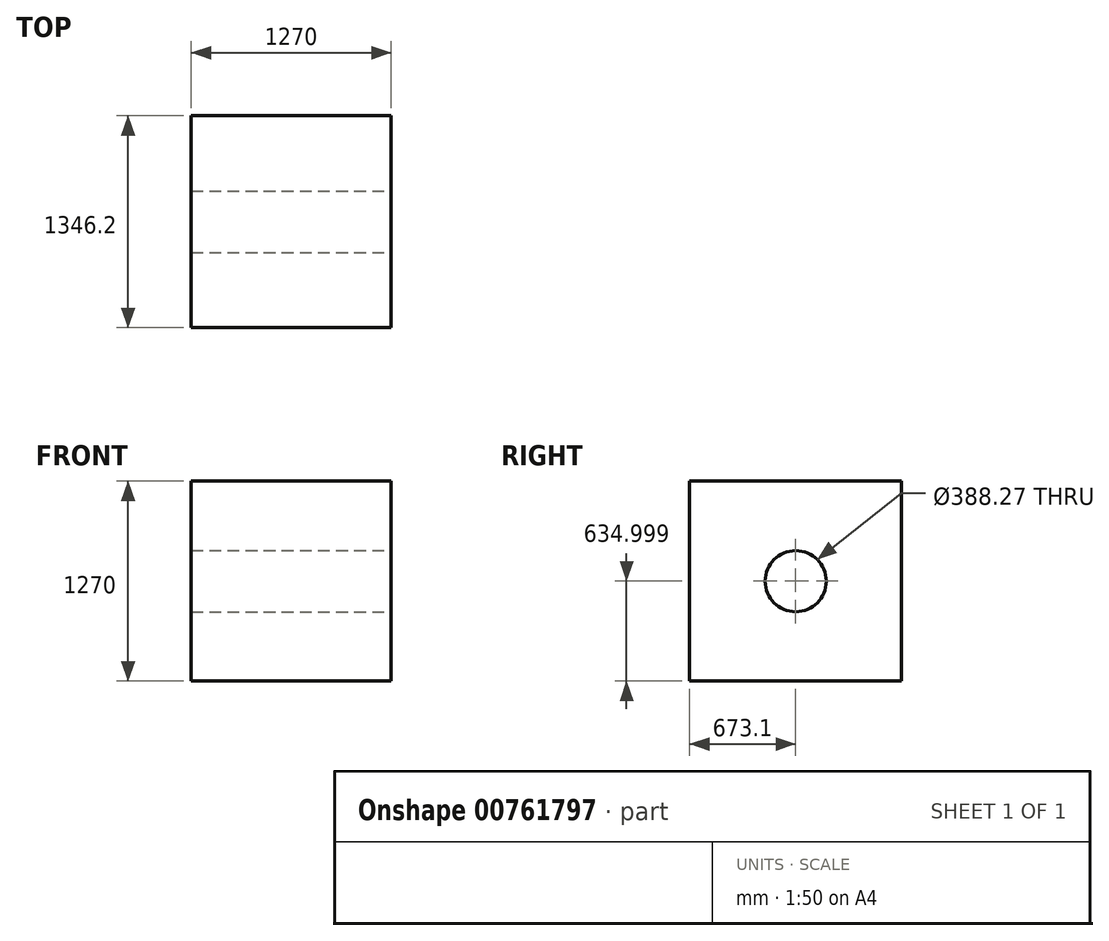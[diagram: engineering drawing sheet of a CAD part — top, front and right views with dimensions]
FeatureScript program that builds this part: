
annotation { "Feature Type Name" : "Feature", "Feature Type Description" : "" }
export const myFeature = defineFeature(function(context is Context, id is Id, definition is map)
    precondition{}
    {
        {
            var Q0;
            Q0=qCreatedBy(makeId("Front.planeOp"),FACE);
            var sketch = newSketch(context, id + "F0", { "sketchPlane" : qUnion([Q0])});
            skLineSegment(sketch, "E0.bottom", {"start": v(-52.99, 1250.98) * mm, "end": v(1217.01, 1250.98) * mm});
            skLineSegment(sketch, "E0.top", {"start": v(-52.99, -19.02) * mm, "end": v(1217.01, -19.02) * mm});
            skLineSegment(sketch, "E0.left", {"start": v(-52.99, 1250.98) * mm, "end": v(-52.99, -19.02) * mm});
            skLineSegment(sketch, "E0.right", {"start": v(1217.01, 1250.98) * mm, "end": v(1217.01, -19.02) * mm});
            skSolve(sketch);
        }
        {
            var Q0;
            Q0=makeQuery(id+"F0.imprint","IMPRINT",FACE,{"disambiguationData":[TD([[makeQuery(id+"F0.imprint","IMPRINT",EDGE,{"derivedFrom":sQuery(id+"F0.wireOp",EDGE,"E0.bottom")}),-1.0]])]});
            extrude(context, id + "F1", {"entities" : qUnion([Q0]), "depth" : 76.2 * mm, "offsetDistance" : 25.4 * mm});
        }
        {
            var Q0;
            Q0=makeQuery(id+"F1.opExtrude","CAP_FACE",FACE,{"disambiguationData":[OSD([sQuery(id+"F0.wireOp",EDGE,"E0.bottom"),sQuery(id+"F0.wireOp",EDGE,"E0.top"),sQuery(id+"F0.wireOp",EDGE,"E0.left"),sQuery(id+"F0.wireOp",EDGE,"E0.right")])],"isStart":true});
            var Q1;
            Q1=makeQuery(id+"F1.opExtrude","CAP_FACE",FACE,{"disambiguationData":[OSD([sQuery(id+"F0.wireOp",EDGE,"E0.bottom"),sQuery(id+"F0.wireOp",EDGE,"E0.top"),sQuery(id+"F0.wireOp",EDGE,"E0.left"),sQuery(id+"F0.wireOp",EDGE,"E0.right")])],"isStart":false});
            extrude(context, id + "F2", {"entities" : qUnion([Q0, Q1]), "operationType" : NewBodyOperationType.ADD, "depth" : 1270 * mm, "offsetDistance" : 25.4 * mm});
        }
        {
            var Q0;
            {var subQ0=sQuery(id+"F0.wireOp",EDGE,"E0.right");Q0=makeQuery(id+"F2.boolean.opBoolean","MERGE",FACE,{"derivedFrom":[makeQuery(id+"F1.opExtrude","SWEPT_FACE",FACE,{"disambiguationData":[OSD([subQ0])]}),makeQuery(id+"F2.opExtrude","SWEPT_FACE",FACE,{"disambiguationData":[OSD([subQ0]),TDD([makeQuery(id+"F1.opExtrude","CAP_EDGE",EDGE,{"disambiguationData":[OSD([subQ0])],"isStart":true})])]}),makeQuery(id+"F2.opExtrude","SWEPT_FACE",FACE,{"disambiguationData":[OSD([subQ0]),TDD([makeQuery(id+"F1.opExtrude","CAP_EDGE",EDGE,{"disambiguationData":[OSD([subQ0])],"isStart":false})])]})]});}
            var sketch = newSketch(context, id + "F3", { "sketchPlane" : qUnion([Q0])});
            skCircle(sketch, "E1", {"center": v(596.9, 615.98) * mm, "radius": 194.14 * mm});
            skPoint(sketch, "E1.centerSnap0", {"position": v(1270, 615.98) * mm});
            skPoint(sketch, "E1.centerSnap1", {"position": v(596.9, 1250.98) * mm});
            skSolve(sketch);
        }
        {
            var Q0;
            Q0=makeQuery(id+"F3.imprint","IMPRINT",FACE,{"disambiguationData":[TD([[makeQuery(id+"F3.imprint","IMPRINT",EDGE,{"derivedFrom":sQuery(id+"F3.wireOp",EDGE,"E1")}),1.0]])]});
            extrude(context, id + "F4", {"entities" : qUnion([Q0]), "operationType" : NewBodyOperationType.ADD, "depth" : 40.64 * mm, "offsetDistance" : 25.4 * mm});
        }
        {
            var Q0;
            Q0=makeQuery(id+"F4.opExtrude","CAP_FACE",FACE,{"disambiguationData":[OSD([sQuery(id+"F3.wireOp",EDGE,"E1")])],"isStart":false});
            extrude(context, id + "F5", {"entities" : qUnion([Q0]), "operationType" : NewBodyOperationType.REMOVE, "oppositeDirection" : true, "depth" : 1397 * mm, "offsetDistance" : 25.4 * mm});
        }
    });
